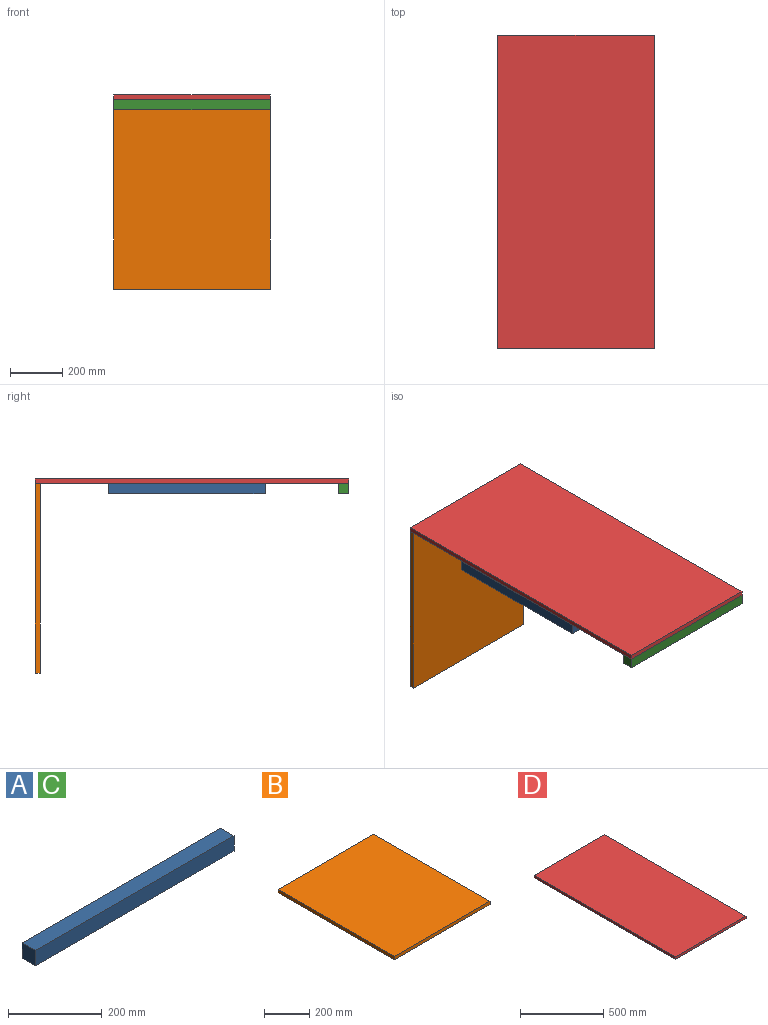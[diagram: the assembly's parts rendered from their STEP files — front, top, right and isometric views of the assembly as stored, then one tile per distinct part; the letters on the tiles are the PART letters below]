
ASSEMBLY  parts=4 mates=8
PART A: 6 faces, bbox 600x40x40 mm
  f0: plane 600x40mm, normal (0,0,1), area 24000mm2, adj f1,f3,f4,f5
  f1: plane 40x40mm, normal (-1,0,0), area 1600mm2, adj f0,f2,f4,f5
  f2: plane 600x40mm, normal (0,0,-1), area 24000mm2, adj f1,f3,f4,f5
  f3: plane 40x40mm, normal (1,0,0), area 1600mm2, adj f0,f2,f4,f5
  f4: plane 600x40mm, normal (0,-1,0), area 24000mm2, adj f0,f1,f2,f3
  f5: plane 600x40mm, normal (0,1,0), area 24000mm2, adj f0,f1,f2,f3
PART B: 6 faces, bbox 600x727x18 mm
  f0: plane 727x600mm, normal (0,0,1), area 436200mm2, adj f1,f3,f4,f5
  f1: plane 727x18mm, normal (-1,0,0), area 13086mm2, adj f0,f2,f4,f5
  f2: plane 727x600mm, normal (0,0,-1), area 436200mm2, adj f1,f3,f4,f5
  f3: plane 727x18mm, normal (1,0,0), area 13086mm2, adj f0,f2,f4,f5
  f4: plane 600x18mm, normal (0,-1,0), area 10800mm2, adj f0,f1,f2,f3
  f5: plane 600x18mm, normal (0,1,0), area 10800mm2, adj f0,f1,f2,f3
PART C: same geometry as A
PART D: 6 faces, bbox 600x1200x18 mm
  f0: plane 1200x600mm, normal (0,0,1), area 720000mm2, adj f1,f3,f4,f5
  f1: plane 1200x18mm, normal (-1,0,0), area 21600mm2, adj f0,f2,f4,f5
  f2: plane 1200x600mm, normal (0,0,-1), area 720000mm2, adj f1,f3,f4,f5
  f3: plane 1200x18mm, normal (1,0,0), area 21600mm2, adj f0,f2,f4,f5
  f4: plane 600x18mm, normal (0,-1,0), area 10800mm2, adj f0,f1,f2,f3
  f5: plane 600x18mm, normal (0,1,0), area 10800mm2, adj f0,f1,f2,f3
PLACE A rot(axis=(0,0,-1),90deg) t=(-280,20,-38)mm
PLACE B rot(axis=(-1,0,0),90deg) t=(0,591,-381.5)mm
PLACE C t=(0,-580,-38)mm
PLACE D t=(0,0,-9)mm
MATE planar B.f3 <-> D.f3  axis (1,0,0) through (300,591,-381.5)mm
MATE planar B.f0 <-> D.f5  axis (0,1,0) through (0,600,-381.5)mm
MATE planar A.f4 <-> D.f1  axis (-1,0,0) through (-300,20,-38)mm
MATE planar C.f0 <-> D.f2  axis (0,0,1) through (0,-580,-18)mm
MATE planar C.f3 <-> D.f3  axis (1,0,0) through (300,-580,-38)mm
MATE planar B.f4 <-> D.f2  axis (0,0,1) through (0,591,-18)mm
MATE planar A.f0 <-> D.f2  axis (0,0,1) through (-280,20,-18)mm
MATE planar C.f4 <-> D.f4  axis (0,-1,0) through (0,-600,-38)mm
